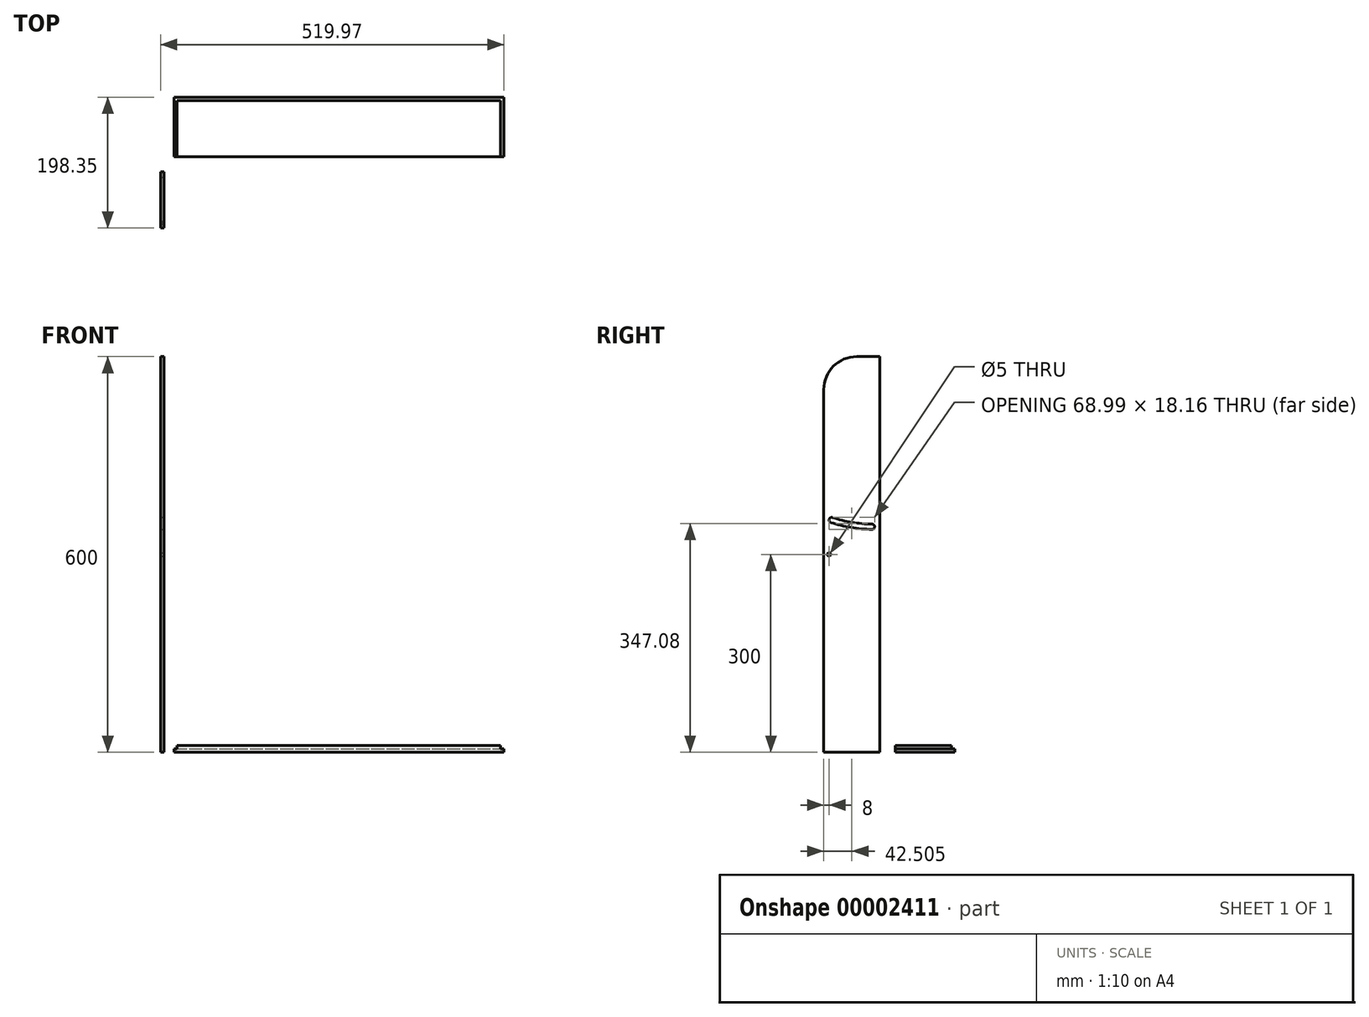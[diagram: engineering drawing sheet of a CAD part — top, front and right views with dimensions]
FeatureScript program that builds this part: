
annotation { "Feature Type Name" : "Feature", "Feature Type Description" : "" }
export const myFeature = defineFeature(function(context is Context, id is Id, definition is map)
    precondition{}
    {
        {
            var Q0;
            Q0=qCreatedBy(makeId("Right.planeOp"),FACE);
            var sketch = newSketch(context, id + "F0", { "sketchPlane" : qUnion([Q0])});
            skLineSegment(sketch, "E0.bottom", {"start": v(0, 0) * mm, "end": v(-85, 0) * mm});
            skLineSegment(sketch, "E0.top", {"start": v(0, 600) * mm, "end": v(-35, 600) * mm});
            skLineSegment(sketch, "E0.left", {"start": v(0, 0) * mm, "end": v(0, 600) * mm});
            skLineSegment(sketch, "E0.right", {"start": v(-85, 0) * mm, "end": v(-85, 550) * mm});
            skPoint(sketch, "E1.visualSharp", {"position": v(-85, 600) * mm});
            skArc(sketch, "E1.filletArc", {"start": v(-35, 600) * mm, "mid": v(-70.36, 585.36) * mm, "end": v(-85, 550) * mm});
            skSolve(sketch);
        }
        {
            var Q0;
            Q0=makeQuery(id+"F0.imprint","IMPRINT",FACE,{"disambiguationData":[TD([[makeQuery(id+"F0.imprint","IMPRINT",EDGE,{"derivedFrom":sQuery(id+"F0.wireOp",EDGE,"E0.bottom")}),-1.0]])]});
            extrude(context, id + "F1", {"entities" : qUnion([Q0]), "depth" : 5 * mm});
        }
        {
            var Q0;
            Q0=qCreatedBy(makeId("Top.planeOp"),FACE);
            var sketch = newSketch(context, id + "F2", { "sketchPlane" : qUnion([Q0])});
            skLineSegment(sketch, "E2.bottom", {"start": v(19.97, 23.35) * mm, "end": v(519.97, 23.35) * mm});
            skLineSegment(sketch, "E2.top", {"start": v(19.97, 113.35) * mm, "end": v(519.97, 113.35) * mm});
            skLineSegment(sketch, "E2.left", {"start": v(19.97, 23.35) * mm, "end": v(19.97, 113.35) * mm});
            skLineSegment(sketch, "E2.right", {"start": v(519.97, 23.35) * mm, "end": v(519.97, 113.35) * mm});
            skSolve(sketch);
        }
        {
            var Q0;
            Q0=makeQuery(id+"F2.imprint","IMPRINT",FACE,{"disambiguationData":[TD([[makeQuery(id+"F2.imprint","IMPRINT",EDGE,{"derivedFrom":sQuery(id+"F2.wireOp",EDGE,"E2.bottom")}),1.0]])]});
            extrude(context, id + "F3", {"entities" : qUnion([Q0]), "depth" : 10 * mm});
        }
        {
            var Q0;
            Q0=makeQuery(id+"F3.opExtrude","CAP_FACE",FACE,{"disambiguationData":[OSD([sQuery(id+"F2.wireOp",EDGE,"E2.bottom"),sQuery(id+"F2.wireOp",EDGE,"E2.top"),sQuery(id+"F2.wireOp",EDGE,"E2.left"),sQuery(id+"F2.wireOp",EDGE,"E2.right")])],"isStart":false});
            var sketch = newSketch(context, id + "F4", { "sketchPlane" : qUnion([Q0])});
            skLineSegment(sketch, "E3", {"start": v(19.97, 23.35) * mm, "end": v(24.97, 23.35) * mm});
            skLineSegment(sketch, "E4", {"start": v(24.97, 23.35) * mm, "end": v(24.97, 108.35) * mm});
            skLineSegment(sketch, "E5", {"start": v(24.97, 108.35) * mm, "end": v(514.97, 108.35) * mm});
            skLineSegment(sketch, "E6", {"start": v(514.97, 108.35) * mm, "end": v(514.97, 23.35) * mm});
            skLineSegment(sketch, "E7", {"start": v(514.97, 23.35) * mm, "end": v(519.97, 23.35) * mm});
            skLineSegment(sketch, "E8", {"start": v(519.97, 23.35) * mm, "end": v(519.97, 113.35) * mm});
            skLineSegment(sketch, "E9", {"start": v(519.97, 113.35) * mm, "end": v(19.97, 113.35) * mm});
            skLineSegment(sketch, "E10", {"start": v(19.97, 113.35) * mm, "end": v(19.97, 23.35) * mm});
            skSolve(sketch);
        }
        {
            var Q0;
            Q0=makeQuery(id+"F4.imprint","IMPRINT",FACE,{"disambiguationData":[TD([[makeQuery(id+"F4.imprint","IMPRINT",EDGE,{"derivedFrom":sQuery(id+"F4.wireOp",EDGE,"E3")}),1.0]])]});
            extrude(context, id + "F5", {"entities" : qUnion([Q0]), "operationType" : NewBodyOperationType.REMOVE, "oppositeDirection" : true, "depth" : 5 * mm});
        }
        {
            var Q0;
            Q0=makeQuery(id+"F1.opExtrude","CAP_FACE",FACE,{"disambiguationData":[OSD([sQuery(id+"F0.wireOp",EDGE,"E0.bottom"),sQuery(id+"F0.wireOp",EDGE,"E0.top"),sQuery(id+"F0.wireOp",EDGE,"E0.left"),sQuery(id+"F0.wireOp",EDGE,"E0.right")])],"isStart":false});
            var sketch = newSketch(context, id + "F6", { "sketchPlane" : qUnion([Q0])});
            skCircle(sketch, "E11", {"center": v(-77, 300) * mm, "radius": 2.5 * mm});
            skArc(sketch, "E12", {"start": v(-71.74, 355.97) * mm, "mid": v(-76.8, 353.43) * mm, "end": v(-74.26, 348.37) * mm});
            skArc(sketch, "E13", {"start": v(-74.26, 348.37) * mm, "mid": v(-43.55, 340.77) * mm, "end": v(-12.04, 338) * mm});
            skArc(sketch, "E14", {"start": v(-12.04, 338) * mm, "mid": v(-8, 341.96) * mm, "end": v(-11.96, 346) * mm});
            skArc(sketch, "E15", {"start": v(-11.96, 346) * mm, "mid": v(-42.24, 348.66) * mm, "end": v(-71.74, 355.97) * mm});
            skArc(sketch, "E16", {"start": v(-110, 368.78) * mm, "mid": v(-44.6, 345) * mm, "end": v(25, 345.08) * mm, "construction": true});
            skSolve(sketch);
        }
        {
            var Q0;
            Q0=makeQuery(id+"F6.imprint","IMPRINT",FACE,{"disambiguationData":[TD([[makeQuery(id+"F6.imprint","IMPRINT",EDGE,{"derivedFrom":sQuery(id+"F6.wireOp",EDGE,"E12")}),1.0]])]});
            var Q1;
            Q1=makeQuery(id+"F6.imprint","IMPRINT",FACE,{"disambiguationData":[TD([[makeQuery(id+"F6.imprint","IMPRINT",EDGE,{"derivedFrom":sQuery(id+"F6.wireOp",EDGE,"E11")}),1.0]])]});
            extrude(context, id + "F7", {"entities" : qUnion([Q0, Q1]), "operationType" : NewBodyOperationType.REMOVE, "endBound" : BoundingType.THROUGH_ALL, "oppositeDirection" : true, "depth" : 25 * mm});
        }
    });
